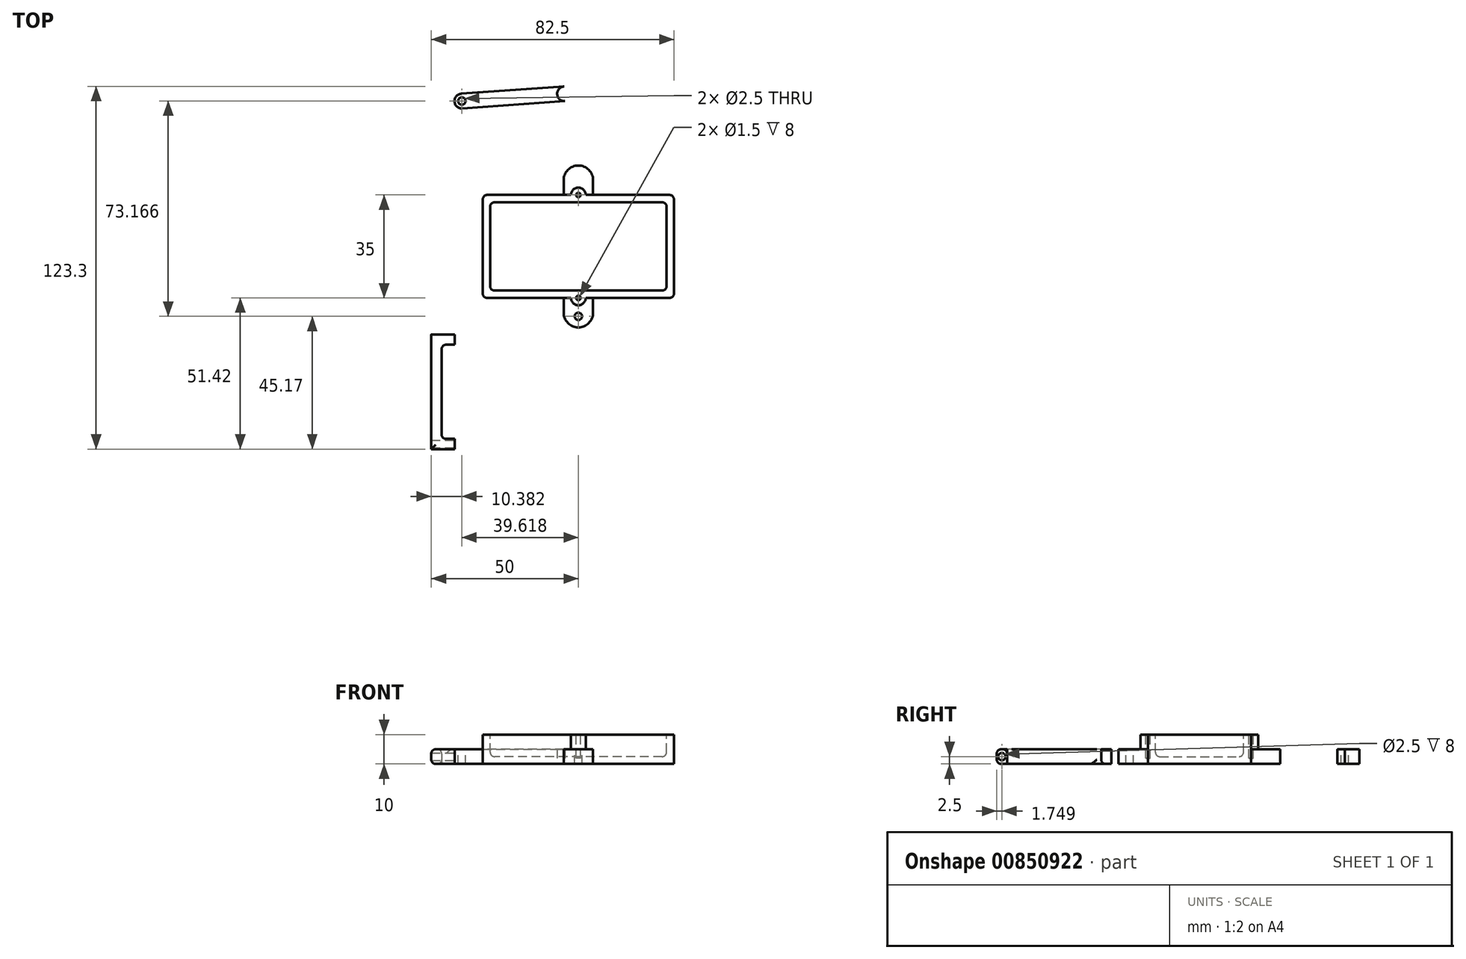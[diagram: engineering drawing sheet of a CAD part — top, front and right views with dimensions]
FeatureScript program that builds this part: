
annotation { "Feature Type Name" : "Feature", "Feature Type Description" : "" }
export const myFeature = defineFeature(function(context is Context, id is Id, definition is map)
    precondition{}
    {
        {
            var Q0;
            Q0=qCreatedBy(makeId("Top.planeOp"),FACE);
            var sketch = newSketch(context, id + "F0", { "sketchPlane" : qUnion([Q0])});
            skLineSegment(sketch, "E0.bottom", {"start": v(32.5, -17.5) * mm, "end": v(-32.5, -17.5) * mm});
            skLineSegment(sketch, "E0.top", {"start": v(32.5, 17.5) * mm, "end": v(-32.5, 17.5) * mm});
            skLineSegment(sketch, "E0.left", {"start": v(32.5, -17.5) * mm, "end": v(32.5, 17.5) * mm});
            skLineSegment(sketch, "E0.right", {"start": v(-32.5, -17.5) * mm, "end": v(-32.5, 17.5) * mm});
            skPoint(sketch, "E0.middle", {"position": v(0, 0) * mm});
            skSolve(sketch);
        }
        {
            var Q0;
            Q0=makeQuery(id+"F0.imprint","IMPRINT",FACE,{"disambiguationData":[TD([[makeQuery(id+"F0.imprint","IMPRINT",EDGE,{"derivedFrom":sQuery(id+"F0.wireOp",EDGE,"E0.bottom")}),-1.0]])]});
            extrude(context, id + "F1", {"entities" : qUnion([Q0]), "depth" : 10 * mm, "offsetDistance" : 25 * mm});
        }
        {
            var Q0;
            Q0=makeQuery(id+"F1.opExtrude","CAP_FACE",FACE,{"disambiguationData":[OSD([sQuery(id+"F0.wireOp",EDGE,"E0.bottom"),sQuery(id+"F0.wireOp",EDGE,"E0.top"),sQuery(id+"F0.wireOp",EDGE,"E0.left"),sQuery(id+"F0.wireOp",EDGE,"E0.right")])],"isStart":false});
            var sketch = newSketch(context, id + "F2", { "sketchPlane" : qUnion([Q0])});
            skLineSegment(sketch, "E1.bottom", {"start": v(30, -15) * mm, "end": v(-30, -15) * mm});
            skLineSegment(sketch, "E1.top", {"start": v(30, 15) * mm, "end": v(-30, 15) * mm});
            skLineSegment(sketch, "E1.left", {"start": v(30, -15) * mm, "end": v(30, 15) * mm});
            skLineSegment(sketch, "E1.right", {"start": v(-30, -15) * mm, "end": v(-30, 15) * mm});
            skPoint(sketch, "E1.middle", {"position": v(0, 0) * mm});
            skSolve(sketch);
        }
        {
            var Q0;
            Q0=makeQuery(id+"F2.imprint","IMPRINT",FACE,{"disambiguationData":[TD([[makeQuery(id+"F2.imprint","IMPRINT",EDGE,{"derivedFrom":sQuery(id+"F2.wireOp",EDGE,"E1.bottom")}),-1.0]])]});
            extrude(context, id + "F3", {"entities" : qUnion([Q0]), "operationType" : NewBodyOperationType.REMOVE, "oppositeDirection" : true, "depth" : 7.5 * mm, "offsetDistance" : 25 * mm});
        }
        {
            var Q0;
            Q0=makeQuery(id+"F1.opExtrude","SWEPT_FACE",FACE,{"disambiguationData":[OSD([sQuery(id+"F0.wireOp",EDGE,"E0.bottom")])]});
            var sketch = newSketch(context, id + "F4", { "sketchPlane" : qUnion([Q0])});
            skLineSegment(sketch, "E2.bottom", {"start": v(0, 0) * mm, "end": v(5, 0) * mm});
            skLineSegment(sketch, "E2.top", {"start": v(0, 5) * mm, "end": v(5, 5) * mm});
            skLineSegment(sketch, "E2.left", {"start": v(0, 0) * mm, "end": v(0, 5) * mm});
            skLineSegment(sketch, "E2.right", {"start": v(5, 0) * mm, "end": v(5, 5) * mm});
            skLineSegment(sketch, "E3.MirrorCS", {"start": v(0, 5) * mm, "end": v(-5, 5) * mm});
            skLineSegment(sketch, "E4.MirrorCS", {"start": v(-5, 0) * mm, "end": v(-5, 5) * mm});
            skLineSegment(sketch, "E5.MirrorCS", {"start": v(0, 0) * mm, "end": v(-5, 0) * mm});
            skSolve(sketch);
        }
        {
            var Q0;
            Q0=makeQuery(id+"F1.opExtrude","SWEPT_FACE",FACE,{"disambiguationData":[OSD([sQuery(id+"F0.wireOp",EDGE,"E0.top")])]});
            var sketch = newSketch(context, id + "F5", { "sketchPlane" : qUnion([Q0])});
            skLineSegment(sketch, "E6.bottom", {"start": v(0, 0) * mm, "end": v(5, 0) * mm});
            skLineSegment(sketch, "E6.top", {"start": v(0, 5) * mm, "end": v(5, 5) * mm});
            skLineSegment(sketch, "E6.left", {"start": v(0, 0) * mm, "end": v(0, 5) * mm});
            skLineSegment(sketch, "E6.right", {"start": v(5, 0) * mm, "end": v(5, 5) * mm});
            skLineSegment(sketch, "E7.MirrorCS", {"start": v(0, 5) * mm, "end": v(-5, 5) * mm});
            skLineSegment(sketch, "E8.MirrorCS", {"start": v(-5, 0) * mm, "end": v(-5, 5) * mm});
            skLineSegment(sketch, "E9.MirrorCS", {"start": v(0, 0) * mm, "end": v(-5, 0) * mm});
            skSolve(sketch);
        }
        {
            var Q0;
            Q0=makeQuery(id+"F5.imprint","IMPRINT",FACE,{"disambiguationData":[TD([[makeQuery(id+"F5.imprint","IMPRINT",EDGE,{"derivedFrom":sQuery(id+"F5.wireOp",EDGE,"E6.left")}),1.0]])]});
            var Q1;
            Q1=makeQuery(id+"F5.imprint","IMPRINT",FACE,{"disambiguationData":[TD([[makeQuery(id+"F5.imprint","IMPRINT",EDGE,{"derivedFrom":sQuery(id+"F5.wireOp",EDGE,"E6.bottom")}),1.0]])]});
            extrude(context, id + "F6", {"entities" : qUnion([Q0, Q1]), "operationType" : NewBodyOperationType.ADD, "depth" : 10 * mm, "offsetDistance" : 25 * mm});
        }
        {
            var Q0;
            Q0=makeQuery(id+"F4.imprint","IMPRINT",FACE,{"disambiguationData":[TD([[makeQuery(id+"F4.imprint","IMPRINT",EDGE,{"derivedFrom":sQuery(id+"F4.wireOp",EDGE,"E2.left")}),1.0]])]});
            var Q1;
            Q1=makeQuery(id+"F4.imprint","IMPRINT",FACE,{"disambiguationData":[TD([[makeQuery(id+"F4.imprint","IMPRINT",EDGE,{"derivedFrom":sQuery(id+"F4.wireOp",EDGE,"E2.bottom")}),-1.0]])]});
            extrude(context, id + "F7", {"entities" : qUnion([Q0, Q1]), "operationType" : NewBodyOperationType.ADD, "depth" : 10 * mm, "offsetDistance" : 25 * mm});
        }
        {
            var Q0;
            Q0=makeQuery(id+"F6.opExtrude","SWEPT_FACE",FACE,{"disambiguationData":[OSD([sQuery(id+"F5.wireOp",EDGE,"E6.top"),sQuery(id+"F5.wireOp",EDGE,"E7.MirrorCS")])]});
            var sketch = newSketch(context, id + "F8", { "sketchPlane" : qUnion([Q0])});
            skCircle(sketch, "E10", {"center": v(0, 17.5) * mm, "radius": 2.5 * mm});
            skSolve(sketch);
        }
        {
            var Q0;
            Q0=makeQuery(id+"F7.opExtrude","SWEPT_FACE",FACE,{"disambiguationData":[OSD([sQuery(id+"F4.wireOp",EDGE,"E2.top"),sQuery(id+"F4.wireOp",EDGE,"E3.MirrorCS")])]});
            var sketch = newSketch(context, id + "F9", { "sketchPlane" : qUnion([Q0])});
            skCircle(sketch, "E11", {"center": v(0, -17.5) * mm, "radius": 2.5 * mm});
            skSolve(sketch);
        }
        {
            var Q0;
            {var subQ0=sQuery(id+"F8.wireOp",EDGE,"E10");var subQ1=makeQuery(id+"F6.opExtrude","CAP_EDGE",EDGE,{"disambiguationData":[OSD([sQuery(id+"F5.wireOp",EDGE,"E6.top"),sQuery(id+"F5.wireOp",EDGE,"E7.MirrorCS")])],"isStart":true});var subQ2=makeQuery(id+"F8.imprint","INTERSECT",VERTEX,{"disambiguationData":[OD(0.0)],"derivedFrom":[subQ1,subQ0]});Q0=makeQuery(id+"F8.imprint","IMPRINT",FACE,{"disambiguationData":[TD([[makeQuery(id+"F8.imprint","IMPRINT",EDGE,{"disambiguationData":[TD([[subQ2,1.0]])],"derivedFrom":subQ0}),1.0]])]});}
            var Q1;
            {var subQ0=sQuery(id+"F9.wireOp",EDGE,"E11");var subQ1=makeQuery(id+"F7.opExtrude","CAP_EDGE",EDGE,{"disambiguationData":[OSD([sQuery(id+"F4.wireOp",EDGE,"E2.top"),sQuery(id+"F4.wireOp",EDGE,"E3.MirrorCS")])],"isStart":true});var subQ2=makeQuery(id+"F9.imprint","INTERSECT",VERTEX,{"disambiguationData":[OD(0.0)],"derivedFrom":[subQ1,subQ0]});Q1=makeQuery(id+"F9.imprint","IMPRINT",FACE,{"disambiguationData":[TD([[makeQuery(id+"F9.imprint","IMPRINT",EDGE,{"disambiguationData":[TD([[subQ2,1.0]])],"derivedFrom":subQ0}),1.0]])]});}
            extrude(context, id + "F10", {"entities" : qUnion([Q0, Q1]), "operationType" : NewBodyOperationType.ADD, "depth" : 5 * mm, "offsetDistance" : 25 * mm});
        }
        {
            var Q0;
            Q0=makeQuery(id+"F10.boolean.opBoolean","MERGE",FACE,{"derivedFrom":[makeQuery(id+"F1.opExtrude","CAP_FACE",FACE,{"disambiguationData":[OSD([sQuery(id+"F0.wireOp",EDGE,"E0.bottom"),sQuery(id+"F0.wireOp",EDGE,"E0.top"),sQuery(id+"F0.wireOp",EDGE,"E0.left"),sQuery(id+"F0.wireOp",EDGE,"E0.right")])],"isStart":false}),makeQuery(id+"F10.opExtrude","CAP_FACE",FACE,{"disambiguationData":[OSD([sQuery(id+"F5.wireOp",EDGE,"E6.top"),sQuery(id+"F5.wireOp",EDGE,"E7.MirrorCS"),sQuery(id+"F8.wireOp",EDGE,"E10")])],"isStart":false}),makeQuery(id+"F10.opExtrude","CAP_FACE",FACE,{"disambiguationData":[OSD([sQuery(id+"F4.wireOp",EDGE,"E2.top"),sQuery(id+"F4.wireOp",EDGE,"E3.MirrorCS"),sQuery(id+"F9.wireOp",EDGE,"E11")])],"isStart":false})]});
            var sketch = newSketch(context, id + "F11", { "sketchPlane" : qUnion([Q0])});
            skLineSegment(sketch, "E12", {"start": v(2.5, 17.5) * mm, "end": v(-2.5, 17.5) * mm, "construction": true});
            skLineSegment(sketch, "E13", {"start": v(0, 17.5) * mm, "end": v(0, 20) * mm, "construction": true});
            skLineSegment(sketch, "E14", {"start": v(2.5, -17.5) * mm, "end": v(-2.5, -17.5) * mm, "construction": true});
            skLineSegment(sketch, "E15", {"start": v(0, -20) * mm, "end": v(0, -17.5) * mm, "construction": true});
            skCircle(sketch, "E16", {"center": v(0, -17.5) * mm, "radius": 0.75 * mm});
            skCircle(sketch, "E17", {"center": v(0, 17.5) * mm, "radius": 0.75 * mm});
            skSolve(sketch);
        }
        {
            var Q0;
            Q0=makeQuery(id+"F11.imprint","IMPRINT",FACE,{"disambiguationData":[TD([[makeQuery(id+"F11.imprint","IMPRINT",EDGE,{"derivedFrom":sQuery(id+"F11.wireOp",EDGE,"E17")}),1.0]])]});
            var Q1;
            Q1=makeQuery(id+"F11.imprint","IMPRINT",FACE,{"disambiguationData":[TD([[makeQuery(id+"F11.imprint","IMPRINT",EDGE,{"derivedFrom":sQuery(id+"F11.wireOp",EDGE,"E16")}),1.0]])]});
            extrude(context, id + "F12", {"entities" : qUnion([Q0, Q1]), "operationType" : NewBodyOperationType.REMOVE, "oppositeDirection" : true, "depth" : 8 * mm, "offsetDistance" : 25 * mm});
        }
        {
            var Q0;
            Q0=makeQuery(id+"F7.opExtrude","SWEPT_FACE",FACE,{"disambiguationData":[OSD([sQuery(id+"F4.wireOp",EDGE,"E2.top"),sQuery(id+"F4.wireOp",EDGE,"E3.MirrorCS")])]});
            var sketch = newSketch(context, id + "F13", { "sketchPlane" : qUnion([Q0])});
            skLineSegment(sketch, "E18", {"start": v(0, -20) * mm, "end": v(0, -27.5) * mm, "construction": true});
            skCircle(sketch, "E19", {"center": v(0, -23.75) * mm, "radius": 1.25 * mm});
            skLineSegment(sketch, "E20", {"start": v(29.85, 0) * mm, "end": v(-30.09, 0) * mm, "construction": true});
            skCircle(sketch, "E21.MirrorC", {"center": v(0, 23.75) * mm, "radius": 1.25 * mm});
            skSolve(sketch);
        }
        {
            var Q0;
            Q0=makeQuery(id+"F13.imprint","IMPRINT",FACE,{"disambiguationData":[TD([[makeQuery(id+"F13.imprint","IMPRINT",EDGE,{"derivedFrom":sQuery(id+"F13.wireOp",EDGE,"E19")}),1.0]])]});
            var Q1;
            Q1=makeQuery(id+"F13.imprint","IMPRINT",FACE,{"disambiguationData":[TD([[makeQuery(id+"F13.imprint","IMPRINT",EDGE,{"derivedFrom":sQuery(id+"F13.wireOp",EDGE,"E21.MirrorC")}),-1.0]])]});
            extrude(context, id + "F14", {"entities" : qUnion([Q0, Q1]), "operationType" : NewBodyOperationType.REMOVE, "oppositeDirection" : true, "depth" : 5 * mm, "offsetDistance" : 25 * mm});
        }
        {
            var Q0;
            Q0=makeQuery(id+"F6.opExtrude","CAP_EDGE",EDGE,{"disambiguationData":[OSD([sQuery(id+"F5.wireOp",EDGE,"E6.right")])],"isStart":false});
            var Q1;
            Q1=makeQuery(id+"F6.opExtrude","CAP_EDGE",EDGE,{"disambiguationData":[OSD([sQuery(id+"F5.wireOp",EDGE,"E8.MirrorCS")])],"isStart":false});
            var Q2;
            Q2=makeQuery(id+"F7.opExtrude","CAP_EDGE",EDGE,{"disambiguationData":[OSD([sQuery(id+"F4.wireOp",EDGE,"E4.MirrorCS")])],"isStart":false});
            var Q3;
            Q3=makeQuery(id+"F7.opExtrude","CAP_EDGE",EDGE,{"disambiguationData":[OSD([sQuery(id+"F4.wireOp",EDGE,"E2.right")])],"isStart":false});
            fillet(context, id + "F15", {"entities" : qUnion([Q0, Q1, Q2, Q3]), "radius" : 5 * mm, "tangentPropagation" : true, "allowEdgeOverflow" : false});
        }
        {
            var Q0;
            Q0=makeQuery(id+"F1.opExtrude","SWEPT_EDGE",EDGE,{"disambiguationData":[OSD([sQuery(id+"F0.wireOp",EDGE,"E0.bottom"),sQuery(id+"F0.wireOp",EDGE,"E0.left")])]});
            var Q1;
            Q1=makeQuery(id+"F1.opExtrude","SWEPT_EDGE",EDGE,{"disambiguationData":[OSD([sQuery(id+"F0.wireOp",EDGE,"E0.top"),sQuery(id+"F0.wireOp",EDGE,"E0.left")])]});
            var Q2;
            Q2=makeQuery(id+"F1.opExtrude","SWEPT_EDGE",EDGE,{"disambiguationData":[OSD([sQuery(id+"F0.wireOp",EDGE,"E0.top"),sQuery(id+"F0.wireOp",EDGE,"E0.right")])]});
            var Q3;
            Q3=makeQuery(id+"F1.opExtrude","SWEPT_EDGE",EDGE,{"disambiguationData":[OSD([sQuery(id+"F0.wireOp",EDGE,"E0.bottom"),sQuery(id+"F0.wireOp",EDGE,"E0.right")])]});
            var Q4;
            Q4=makeQuery(id+"F3.boolean.opBoolean","COPY",EDGE,{"derivedFrom":makeQuery(id+"F3.opExtrude","SWEPT_EDGE",EDGE,{"disambiguationData":[OSD([sQuery(id+"F2.wireOp",EDGE,"E1.top"),sQuery(id+"F2.wireOp",EDGE,"E1.right")])]})});
            var Q5;
            Q5=makeQuery(id+"F3.boolean.opBoolean","COPY",EDGE,{"derivedFrom":makeQuery(id+"F3.opExtrude","SWEPT_EDGE",EDGE,{"disambiguationData":[OSD([sQuery(id+"F2.wireOp",EDGE,"E1.top"),sQuery(id+"F2.wireOp",EDGE,"E1.left")])]})});
            var Q6;
            Q6=makeQuery(id+"F3.boolean.opBoolean","COPY",EDGE,{"derivedFrom":makeQuery(id+"F3.opExtrude","SWEPT_EDGE",EDGE,{"disambiguationData":[OSD([sQuery(id+"F2.wireOp",EDGE,"E1.bottom"),sQuery(id+"F2.wireOp",EDGE,"E1.right")])]})});
            var Q7;
            Q7=makeQuery(id+"F3.boolean.opBoolean","COPY",EDGE,{"derivedFrom":makeQuery(id+"F3.opExtrude","SWEPT_EDGE",EDGE,{"disambiguationData":[OSD([sQuery(id+"F2.wireOp",EDGE,"E1.bottom"),sQuery(id+"F2.wireOp",EDGE,"E1.left")])]})});
            var Q8;
            Q8=makeQuery(id+"F3.boolean.opBoolean","COPY",EDGE,{"derivedFrom":makeQuery(id+"F3.opExtrude","CAP_EDGE",EDGE,{"disambiguationData":[OSD([sQuery(id+"F2.wireOp",EDGE,"E1.top")])],"isStart":false})});
            var Q9;
            Q9=makeQuery(id+"F3.boolean.opBoolean","COPY",EDGE,{"derivedFrom":makeQuery(id+"F3.opExtrude","CAP_EDGE",EDGE,{"disambiguationData":[OSD([sQuery(id+"F2.wireOp",EDGE,"E1.right")])],"isStart":false})});
            var Q10;
            Q10=makeQuery(id+"F3.boolean.opBoolean","COPY",EDGE,{"derivedFrom":makeQuery(id+"F3.opExtrude","CAP_EDGE",EDGE,{"disambiguationData":[OSD([sQuery(id+"F2.wireOp",EDGE,"E1.left")])],"isStart":false})});
            var Q11;
            Q11=makeQuery(id+"F3.boolean.opBoolean","COPY",EDGE,{"derivedFrom":makeQuery(id+"F3.opExtrude","CAP_EDGE",EDGE,{"disambiguationData":[OSD([sQuery(id+"F2.wireOp",EDGE,"E1.bottom")])],"isStart":false})});
            fillet(context, id + "F16", {"entities" : qUnion([Q0, Q1, Q2, Q3, Q4, Q5, Q6, Q7, Q8, Q9, Q10, Q11]), "radius" : 1.5 * mm, "tangentPropagation" : true, "allowEdgeOverflow" : false});
        }
        {
            var Q0;
            Q0=qCreatedBy(makeId("Top.planeOp"),FACE);
            var sketch = newSketch(context, id + "F17", { "sketchPlane" : qUnion([Q0])});
            skCircle(sketch, "E22", {"center": v(53.27, 16.57) * mm, "radius": 4.98 * mm});
            skCircle(sketch, "E23", {"center": v(-39.62, 49.42) * mm, "radius": 2.5 * mm});
            skLineSegment(sketch, "E24", {"start": v(-39.62, 49.42) * mm, "end": v(-39.8, 51.9) * mm, "construction": true});
            skLineSegment(sketch, "E25", {"start": v(-39.8, 51.9) * mm, "end": v(-22.34, 53.14) * mm});
            skLineSegment(sketch, "E26", {"start": v(-22.34, 53.14) * mm, "end": v(-21.18, 36.75) * mm, "construction": true});
            skLineSegment(sketch, "E27.MirrorCS", {"start": v(-4.88, 54.38) * mm, "end": v(-22.34, 53.14) * mm});
            skCircle(sketch, "E28.MirrorC", {"center": v(-4.7, 51.88) * mm, "radius": 2.5 * mm});
            skLineSegment(sketch, "E29", {"start": v(-39.62, 49.42) * mm, "end": v(-4.7, 51.88) * mm, "construction": true});
            skLineSegment(sketch, "E30.MirrorCS", {"start": v(-39.44, 46.92) * mm, "end": v(-21.98, 48.16) * mm});
            skLineSegment(sketch, "E31.MirrorCS", {"start": v(-4.53, 49.39) * mm, "end": v(-21.98, 48.16) * mm});
            skSolve(sketch);
        }
        {
            var Q0;
            {var subQ0=sQuery(id+"F17.wireOp",EDGE,"E23");var subQ1=makeQuery(id+"F17.imprint","INTERSECT",VERTEX,{"derivedFrom":[subQ0,sQuery(id+"F17.wireOp",EDGE,"E25")]});Q0=makeQuery(id+"F17.imprint","IMPRINT",FACE,{"disambiguationData":[TD([[makeQuery(id+"F17.imprint","IMPRINT",EDGE,{"disambiguationData":[TD([[subQ1,-1.0]])],"derivedFrom":subQ0}),1.0]])]});}
            var Q1;
            {var subQ0=sQuery(id+"F17.wireOp",EDGE,"E28.MirrorC");var subQ1=makeQuery(id+"F17.imprint","INTERSECT",VERTEX,{"derivedFrom":[sQuery(id+"F17.wireOp",EDGE,"E27.MirrorCS"),subQ0]});Q1=makeQuery(id+"F17.imprint","IMPRINT",FACE,{"disambiguationData":[TD([[makeQuery(id+"F17.imprint","IMPRINT",EDGE,{"disambiguationData":[TD([[subQ1,-1.0]])],"derivedFrom":subQ0}),-1.0]])]});}
            var Q2;
            {var subQ3=sQuery(id+"F17.wireOp",EDGE,"E25");Q2=makeQuery(id+"F17.imprint","IMPRINT",FACE,{"disambiguationData":[TD([[makeQuery(id+"F17.imprint","IMPRINT",EDGE,{"derivedFrom":subQ3}),-1.0]])]});}
            extrude(context, id + "F18", {"entities" : qUnion([Q0, Q1, Q2]), "depth" : 5 * mm, "offsetDistance" : 25 * mm});
        }
        {
            var Q0;
            Q0=makeQuery(id+"F18.opExtrude","CAP_FACE",FACE,{"disambiguationData":[OSD([sQuery(id+"F17.wireOp",EDGE,"E23"),sQuery(id+"F17.wireOp",EDGE,"E25"),sQuery(id+"F17.wireOp",EDGE,"E27.MirrorCS"),sQuery(id+"F17.wireOp",EDGE,"E28.MirrorC"),sQuery(id+"F17.wireOp",EDGE,"E30.MirrorCS"),sQuery(id+"F17.wireOp",EDGE,"E31.MirrorCS")])],"isStart":false});
            var sketch = newSketch(context, id + "F19", { "sketchPlane" : qUnion([Q0])});
            skLineSegment(sketch, "E32", {"start": v(-39.44, 46.92) * mm, "end": v(-39.8, 51.9) * mm, "construction": true});
            skLineSegment(sketch, "E33", {"start": v(-39.62, 49.42) * mm, "end": v(-42.11, 49.24) * mm, "construction": true});
            skCircle(sketch, "E34", {"center": v(-39.62, 49.42) * mm, "radius": 1.25 * mm});
            skLineSegment(sketch, "E35", {"start": v(-21.98, 48.16) * mm, "end": v(-22.34, 53.14) * mm, "construction": true});
            skCircle(sketch, "E36.MirrorC", {"center": v(-4.7, 51.88) * mm, "radius": 1.25 * mm});
            skSolve(sketch);
        }
        {
            var Q0;
            Q0=makeQuery(id+"F19.imprint","IMPRINT",FACE,{"disambiguationData":[TD([[makeQuery(id+"F19.imprint","IMPRINT",EDGE,{"derivedFrom":sQuery(id+"F19.wireOp",EDGE,"E34")}),1.0]])]});
            var Q1;
            Q1=makeQuery(id+"F19.imprint","IMPRINT",FACE,{"disambiguationData":[TD([[makeQuery(id+"F19.imprint","IMPRINT",EDGE,{"derivedFrom":sQuery(id+"F19.wireOp",EDGE,"E36.MirrorC")}),-1.0]])]});
            extrude(context, id + "F20", {"entities" : qUnion([Q0, Q1]), "operationType" : NewBodyOperationType.REMOVE, "oppositeDirection" : true, "depth" : 5 * mm, "offsetDistance" : 25 * mm});
        }
        {
            var Q0;
            Q0=qCreatedBy(makeId("Top.planeOp"),FACE);
            var sketch = newSketch(context, id + "F21", { "sketchPlane" : qUnion([Q0])});
            skLineSegment(sketch, "E37.bottom", {"start": v(-50, -65.42) * mm, "end": v(-46.5, -65.42) * mm});
            skLineSegment(sketch, "E37.top", {"start": v(-50, -33.42) * mm, "end": v(-46.5, -33.42) * mm});
            skLineSegment(sketch, "E37.left", {"start": v(-50, -65.42) * mm, "end": v(-50, -33.42) * mm});
            skLineSegment(sketch, "E37.right", {"start": v(-46.5, -65.42) * mm, "end": v(-46.5, -33.42) * mm});
            skLineSegment(sketch, "E38.bottom", {"start": v(-50, -33.42) * mm, "end": v(-42, -33.42) * mm});
            skLineSegment(sketch, "E38.top", {"start": v(-50, -29.92) * mm, "end": v(-42, -29.92) * mm});
            skLineSegment(sketch, "E38.left", {"start": v(-50, -33.42) * mm, "end": v(-50, -29.92) * mm});
            skLineSegment(sketch, "E38.right", {"start": v(-42, -33.42) * mm, "end": v(-42, -29.92) * mm});
            skLineSegment(sketch, "E39", {"start": v(-50, -49.42) * mm, "end": v(-46.5, -49.42) * mm, "construction": true});
            skLineSegment(sketch, "E40.MirrorCS", {"start": v(-50, -65.42) * mm, "end": v(-42, -65.42) * mm});
            skLineSegment(sketch, "E41.MirrorCS", {"start": v(-50, -68.92) * mm, "end": v(-42, -68.92) * mm});
            skLineSegment(sketch, "E42.MirrorCS", {"start": v(-42, -65.42) * mm, "end": v(-42, -68.92) * mm});
            skLineSegment(sketch, "E43.MirrorCS", {"start": v(-50, -65.42) * mm, "end": v(-50, -68.92) * mm});
            skSolve(sketch);
        }
        {
            var Q0;
            Q0=makeQuery(id+"F21.imprint","IMPRINT",FACE,{"disambiguationData":[TD([[makeQuery(id+"F21.imprint","IMPRINT",EDGE,{"derivedFrom":sQuery(id+"F21.wireOp",EDGE,"E37.bottom")}),-1.0]])]});
            var Q1;
            Q1=makeQuery(id+"F21.imprint","IMPRINT",FACE,{"disambiguationData":[TD([[makeQuery(id+"F21.imprint","IMPRINT",EDGE,{"derivedFrom":sQuery(id+"F21.wireOp",EDGE,"E37.bottom")}),1.0]])]});
            var Q2;
            Q2=makeQuery(id+"F21.imprint","IMPRINT",FACE,{"disambiguationData":[TD([[makeQuery(id+"F21.imprint","IMPRINT",EDGE,{"derivedFrom":sQuery(id+"F21.wireOp",EDGE,"E37.top")}),1.0]])]});
            extrude(context, id + "F22", {"entities" : qUnion([Q0, Q1, Q2]), "depth" : 5 * mm, "offsetDistance" : 25 * mm});
        }
        {
            var Q0;
            Q0=makeQuery(id+"F22.opExtrude","SWEPT_FACE",FACE,{"disambiguationData":[OSD([sQuery(id+"F21.wireOp",EDGE,"E42.MirrorCS")])]});
            var sketch = newSketch(context, id + "F23", { "sketchPlane" : qUnion([Q0])});
            skLineSegment(sketch, "E44", {"start": v(-49.42, 0) * mm, "end": v(-49.42, 5) * mm, "construction": true});
            skLineSegment(sketch, "E45", {"start": v(-65.42, 0) * mm, "end": v(-68.92, 5) * mm, "construction": true});
            skLineSegment(sketch, "E46", {"start": v(-65.42, 5) * mm, "end": v(-68.92, 0) * mm, "construction": true});
            skCircle(sketch, "E47", {"center": v(-67.17, 2.5) * mm, "radius": 1.25 * mm});
            skCircle(sketch, "E48.MirrorC", {"center": v(-31.67, 2.5) * mm, "radius": 1.25 * mm});
            skSolve(sketch);
        }
        {
            var Q0;
            Q0=makeQuery(id+"F23.imprint","IMPRINT",FACE,{"disambiguationData":[TD([[makeQuery(id+"F23.imprint","IMPRINT",EDGE,{"derivedFrom":sQuery(id+"F23.wireOp",EDGE,"E48.MirrorC")}),-1.0]])]});
            var Q1;
            Q1=makeQuery(id+"F23.imprint","IMPRINT",FACE,{"disambiguationData":[TD([[makeQuery(id+"F23.imprint","IMPRINT",EDGE,{"derivedFrom":sQuery(id+"F23.wireOp",EDGE,"E47")}),1.0]])]});
            extrude(context, id + "F24", {"entities" : qUnion([Q0, Q1]), "operationType" : NewBodyOperationType.REMOVE, "oppositeDirection" : true, "depth" : 8 * mm, "offsetDistance" : 25 * mm});
        }
        {
            var Q0;
            Q0=makeQuery(id+"F22.opExtrude","SWEPT_EDGE",EDGE,{"disambiguationData":[OSD([sQuery(id+"F21.wireOp",EDGE,"E37.bottom"),sQuery(id+"F21.wireOp",EDGE,"E37.right"),sQuery(id+"F21.wireOp",EDGE,"E40.MirrorCS")])]});
            var Q1;
            Q1=makeQuery(id+"F22.opExtrude","SWEPT_EDGE",EDGE,{"disambiguationData":[OSD([sQuery(id+"F21.wireOp",EDGE,"E37.top"),sQuery(id+"F21.wireOp",EDGE,"E37.right"),sQuery(id+"F21.wireOp",EDGE,"E38.bottom")])]});
            var Q2;
            Q2=makeQuery(id+"F22.opExtrude","CAP_EDGE",EDGE,{"disambiguationData":[OSD([sQuery(id+"F21.wireOp",EDGE,"E37.right")])],"isStart":false});
            var Q3;
            Q3=makeQuery(id+"F22.opExtrude","CAP_EDGE",EDGE,{"disambiguationData":[OSD([sQuery(id+"F21.wireOp",EDGE,"E37.left"),sQuery(id+"F21.wireOp",EDGE,"E38.left"),sQuery(id+"F21.wireOp",EDGE,"E43.MirrorCS")])],"isStart":false});
            var Q4;
            Q4=makeQuery(id+"F22.opExtrude","CAP_EDGE",EDGE,{"disambiguationData":[OSD([sQuery(id+"F21.wireOp",EDGE,"E41.MirrorCS")])],"isStart":false});
            var Q5;
            Q5=makeQuery(id+"F22.opExtrude","CAP_EDGE",EDGE,{"disambiguationData":[OSD([sQuery(id+"F21.wireOp",EDGE,"E41.MirrorCS")])],"isStart":true});
            var Q6;
            Q6=makeQuery(id+"F22.opExtrude","CAP_EDGE",EDGE,{"disambiguationData":[OSD([sQuery(id+"F21.wireOp",EDGE,"E37.left"),sQuery(id+"F21.wireOp",EDGE,"E38.left"),sQuery(id+"F21.wireOp",EDGE,"E43.MirrorCS")])],"isStart":true});
            var Q7;
            Q7=makeQuery(id+"F22.opExtrude","CAP_EDGE",EDGE,{"disambiguationData":[OSD([sQuery(id+"F21.wireOp",EDGE,"E38.bottom")])],"isStart":true});
            fillet(context, id + "F25", {"entities" : qUnion([Q0, Q1, Q2, Q3, Q4, Q5, Q6, Q7]), "radius" : 1.5 * mm, "tangentPropagation" : true, "allowEdgeOverflow" : false});
        }
    });
